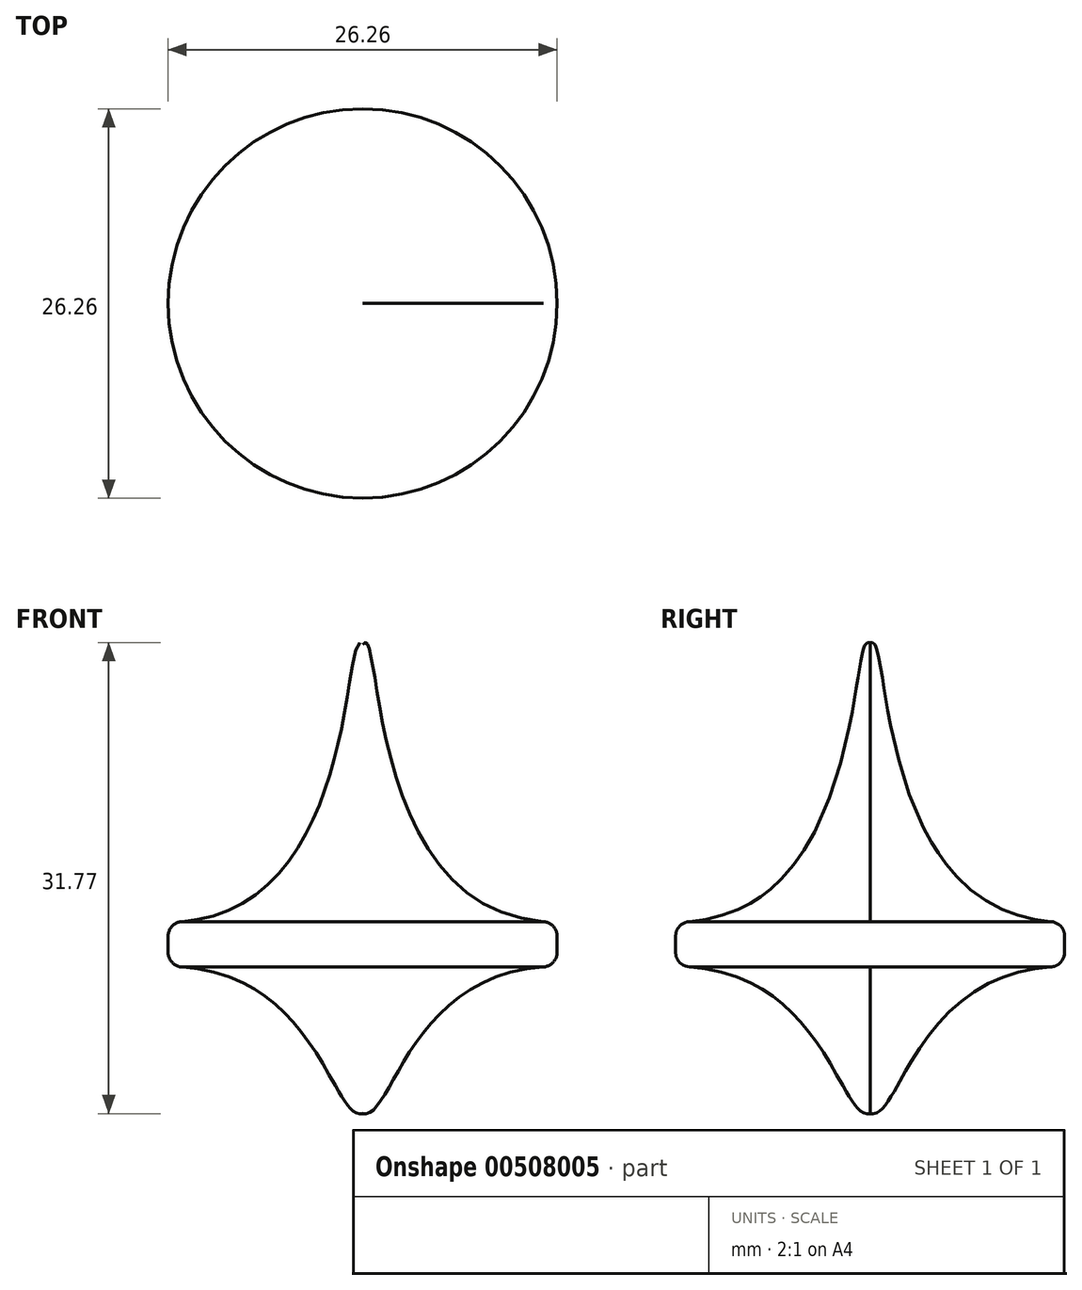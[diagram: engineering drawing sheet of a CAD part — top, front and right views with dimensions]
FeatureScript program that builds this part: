
annotation { "Feature Type Name" : "Feature", "Feature Type Description" : "" }
export const myFeature = defineFeature(function(context is Context, id is Id, definition is map)
    precondition{}
    {
        {
            var Q0;
            Q0=qCreatedBy(makeId("Front.planeOp"),FACE);
            var sketch = newSketch(context, id + "F0", { "sketchPlane" : qUnion([Q0])});
            skLineSegment(sketch, "E0.right", {"start": v(13.13, 0) * mm, "end": v(13.13, -3) * mm});
            skLineSegment(sketch, "E1", {"start": v(0, 18.74) * mm, "end": v(0, -12.88) * mm});
            skFitSpline(sketch, "E2", {"points": [v(13.13, -3) * mm, v(0, -12.88) * mm], "startDerivative": vector(-30.13, 0.1) * mm, "endDerivative": vector(-5.96, 2.3) * mm});
            skFitSpline(sketch, "E3", {"points": [v(0, 18.74) * mm, v(13.13, 0) * mm], "startDerivative": vector(4.28, 5.48) * mm, "endDerivative": vector(39.4, 0) * mm});
            skSolve(sketch);
        }
        {
            var Q0;
            Q0=makeQuery(id+"F0.imprint","IMPRINT",FACE,{"disambiguationData":[TD([[makeQuery(id+"F0.imprint","IMPRINT",EDGE,{"derivedFrom":sQuery(id+"F0.wireOp",EDGE,"E0.right")}),-1.0]])]});
            var Q1;
            Q1=sQuery(id+"F0.wireOp",EDGE,"E1");
            revolve(context, id + "F1", {"entities" : qUnion([Q0]), "axis" : qUnion([Q1]), "revolveType" : RevolveType.ONE_DIRECTION, "angle" : 360 * degree});
        }
        {
            var Q0;
            Q0=makeQuery(id+"F1.opRevolve","SWEPT_EDGE",EDGE,{"disambiguationData":[OSD([sQuery(id+"F0.wireOp",EDGE,"E0.right"),sQuery(id+"F0.wireOp",EDGE,"E3")])]});
            var Q1;
            Q1=makeQuery(id+"F1.opRevolve","SWEPT_EDGE",EDGE,{"disambiguationData":[OSD([sQuery(id+"F0.wireOp",EDGE,"E0.right"),sQuery(id+"F0.wireOp",EDGE,"E2")])]});
            fillet(context, id + "F2", {"entities" : qUnion([Q0, Q1]), "radius" : 1 * mm, "tangentPropagation" : true, "allowEdgeOverflow" : false});
        }
    });
